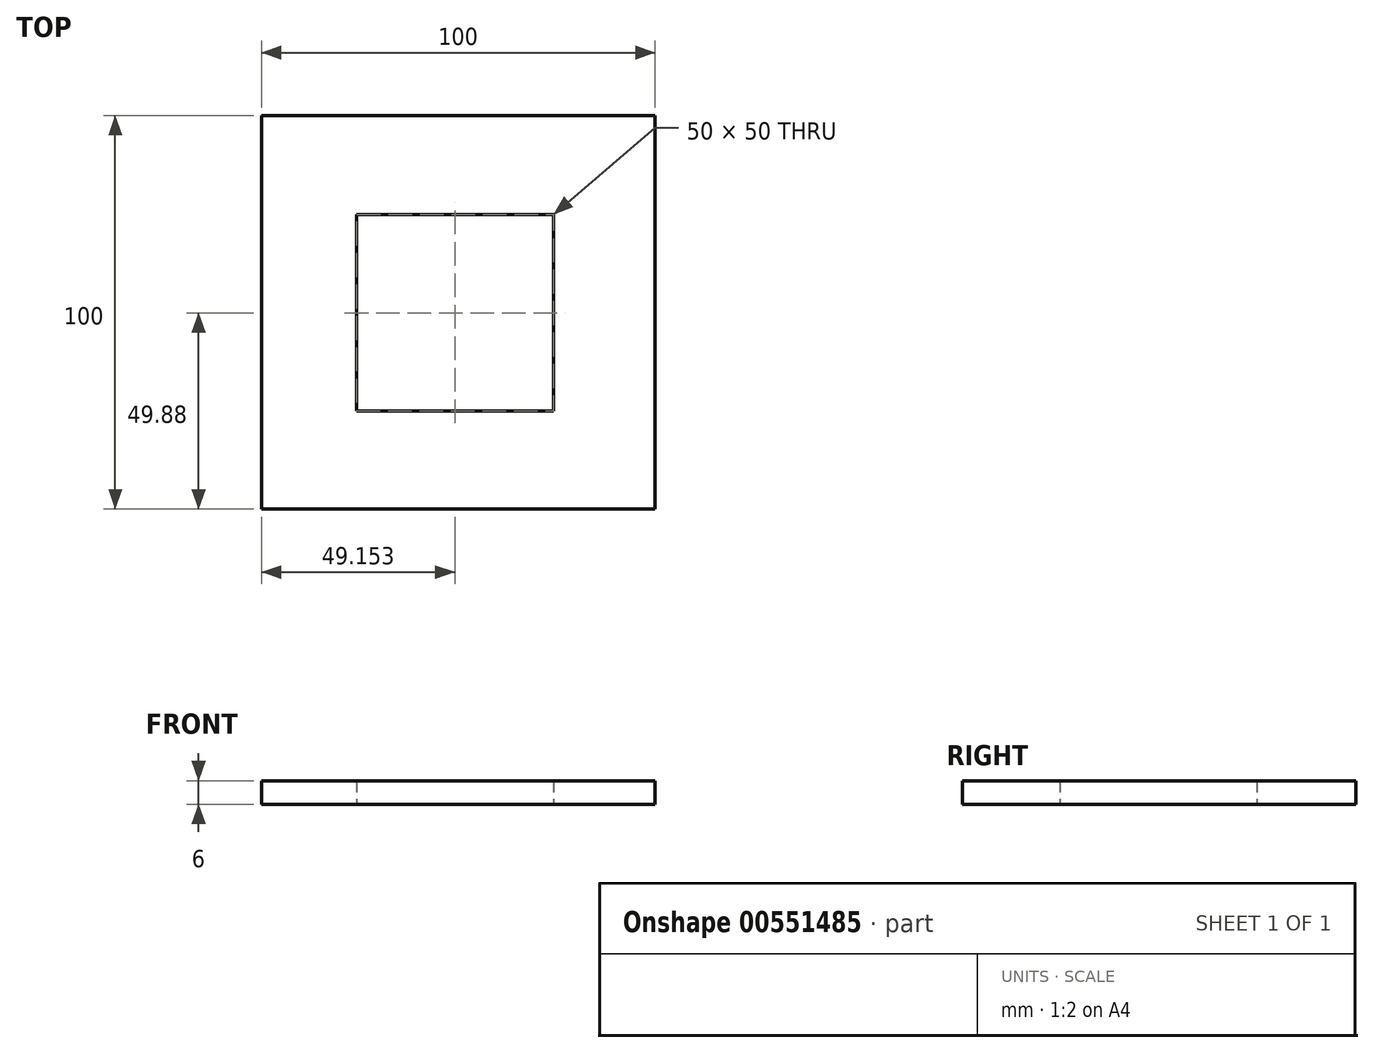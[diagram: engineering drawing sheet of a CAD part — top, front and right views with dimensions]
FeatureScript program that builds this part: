
annotation { "Feature Type Name" : "Feature", "Feature Type Description" : "" }
export const myFeature = defineFeature(function(context is Context, id is Id, definition is map)
    precondition{}
    {
        {
            var Q0;
            Q0=qCreatedBy(makeId("Top.planeOp"),FACE);
            var sketch = newSketch(context, id + "F0", { "sketchPlane" : qUnion([Q0])});
            skLineSegment(sketch, "E0.bottom", {"start": v(-71.5, 75.12) * mm, "end": v(28.5, 75.12) * mm});
            skLineSegment(sketch, "E0.top", {"start": v(-71.5, -24.88) * mm, "end": v(28.5, -24.88) * mm});
            skLineSegment(sketch, "E0.left", {"start": v(-71.5, 75.12) * mm, "end": v(-71.5, -24.88) * mm});
            skLineSegment(sketch, "E0.right", {"start": v(28.5, 75.12) * mm, "end": v(28.5, -24.88) * mm});
            skLineSegment(sketch, "E1.bottom", {"start": v(-47.35, 50) * mm, "end": v(2.65, 50) * mm});
            skLineSegment(sketch, "E1.top", {"start": v(-47.35, 0) * mm, "end": v(2.65, 0) * mm});
            skLineSegment(sketch, "E1.left", {"start": v(-47.35, 50) * mm, "end": v(-47.35, 0) * mm});
            skLineSegment(sketch, "E1.right", {"start": v(2.65, 50) * mm, "end": v(2.65, 0) * mm});
            skSolve(sketch);
        }
        {
            var Q0;
            Q0=makeQuery(id+"F0.imprint","IMPRINT",FACE,{"disambiguationData":[TD([[makeQuery(id+"F0.imprint","IMPRINT",EDGE,{"derivedFrom":sQuery(id+"F0.wireOp",EDGE,"E0.bottom")}),-1.0]])]});
            extrude(context, id + "F1", {"entities" : qUnion([Q0]), "depth" : 6 * mm, "offsetDistance" : 25 * mm});
        }
    });
